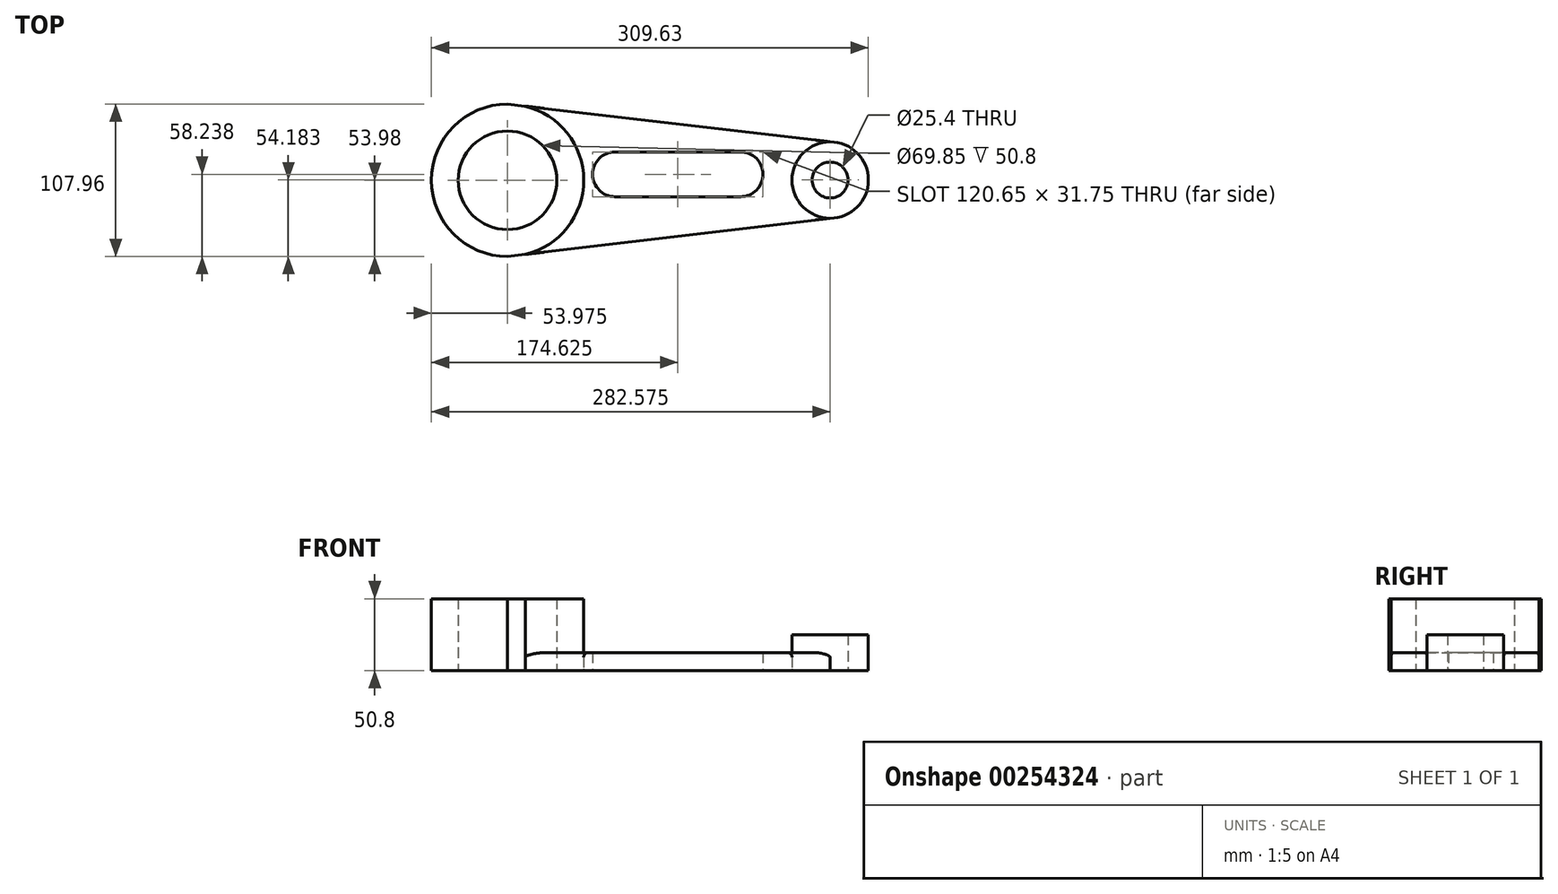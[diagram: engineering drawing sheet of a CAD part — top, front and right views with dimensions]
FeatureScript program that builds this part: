
annotation { "Feature Type Name" : "Feature", "Feature Type Description" : "" }
export const myFeature = defineFeature(function(context is Context, id is Id, definition is map)
    precondition{}
    {
        {
            var Q0;
            Q0=qCreatedBy(makeId("Top.planeOp"),FACE);
            var sketch = newSketch(context, id + "F0", { "sketchPlane" : qUnion([Q0])});
            skCircle(sketch, "E0", {"center": v(-91.28, 0) * mm, "radius": 53.98 * mm});
            skCircle(sketch, "E1", {"center": v(-91.28, 0) * mm, "radius": 34.93 * mm});
            skCircle(sketch, "E2", {"center": v(137.32, 0.2) * mm, "radius": 12.7 * mm});
            skCircle(sketch, "E3", {"center": v(137.32, 0.2) * mm, "radius": 27.05 * mm});
            skArc(sketch, "E4", {"start": v(-15.08, 20.13) * mm, "mid": v(-30.96, 4.26) * mm, "end": v(-15.08, -11.62) * mm});
            skLineSegment(sketch, "E5", {"start": v(-15.08, 20.13) * mm, "end": v(73.82, 20.13) * mm});
            skLineSegment(sketch, "E6", {"start": v(-15.08, -11.62) * mm, "end": v(73.82, -11.62) * mm});
            skArc(sketch, "E7", {"start": v(73.82, -11.62) * mm, "mid": v(89.7, 4.26) * mm, "end": v(73.82, 20.13) * mm});
            skLineSegment(sketch, "E8", {"start": v(-91.28, 53.98) * mm, "end": v(137.32, 27.25) * mm});
            skLineSegment(sketch, "E9", {"start": v(-91.28, -53.97) * mm, "end": v(137.32, -26.85) * mm});
            skSolve(sketch);
        }
        {
            var Q0;
            Q0=makeQuery(id+"F0.imprint","IMPRINT",FACE,{"disambiguationData":[TD([[makeQuery(id+"F0.imprint","IMPRINT",EDGE,{"derivedFrom":sQuery(id+"F0.wireOp",EDGE,"E1")}),-1.0]])]});
            extrude(context, id + "F1", {"entities" : qUnion([Q0]), "depth" : 50.8 * mm});
        }
        {
            var Q0;
            Q0=makeQuery(id+"F0.imprint","IMPRINT",FACE,{"disambiguationData":[TD([[makeQuery(id+"F0.imprint","IMPRINT",EDGE,{"derivedFrom":sQuery(id+"F0.wireOp",EDGE,"E2")}),-1.0]])]});
            extrude(context, id + "F2", {"entities" : qUnion([Q0]), "depth" : 25.4 * mm});
        }
        {
            var Q0;
            Q0=makeQuery(id+"F0.imprint","IMPRINT",FACE,{"disambiguationData":[TD([[makeQuery(id+"F0.imprint","IMPRINT",EDGE,{"derivedFrom":sQuery(id+"F0.wireOp",EDGE,"E4")}),-1.0]])]});
            extrude(context, id + "F3", {"entities" : qUnion([Q0]), "depth" : 12.7 * mm});
        }
        {
            var Q0;
            Q0=makeQuery(id+"F3.opExtrude","CAP_EDGE",EDGE,{"disambiguationData":[OSD([sQuery(id+"F0.wireOp",EDGE,"E0")])],"isStart":false});
            var Q1;
            Q1=makeQuery(id+"F3.opExtrude","CAP_EDGE",EDGE,{"disambiguationData":[OSD([sQuery(id+"F0.wireOp",EDGE,"E3")])],"isStart":false});
            fillet(context, id + "F4", {"entities" : qUnion([Q0, Q1]), "radius" : 3.17 * mm, "tangentPropagation" : true, "allowEdgeOverflow" : false});
        }
    });
